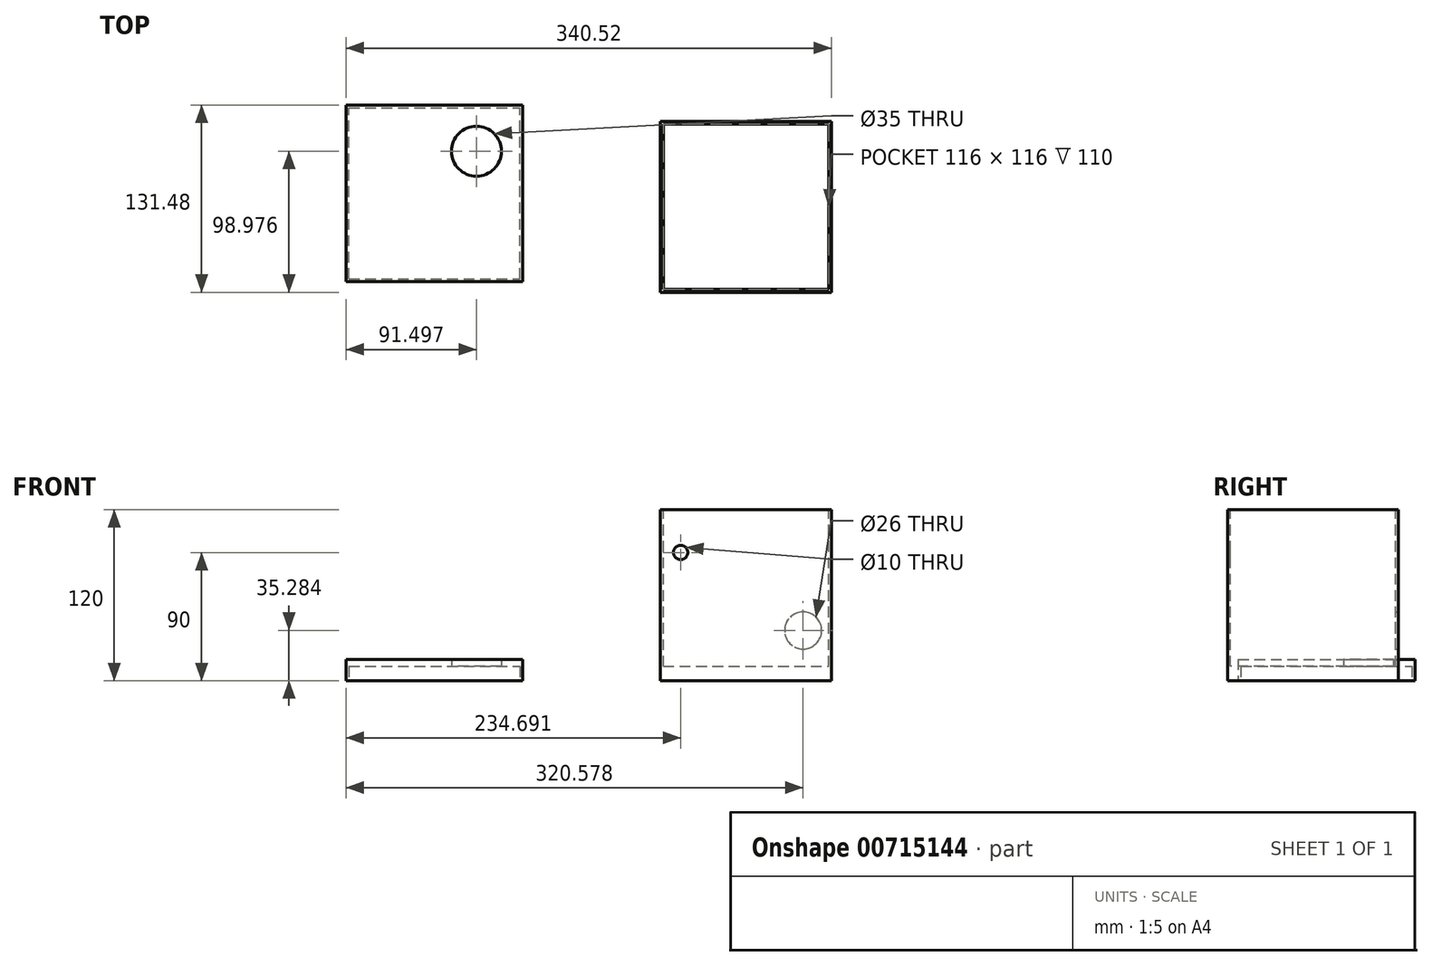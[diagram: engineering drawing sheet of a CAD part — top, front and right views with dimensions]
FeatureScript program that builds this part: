
annotation { "Feature Type Name" : "Feature", "Feature Type Description" : "" }
export const myFeature = defineFeature(function(context is Context, id is Id, definition is map)
    precondition{}
    {
        {
            var Q0;
            Q0=qCreatedBy(makeId("Top.planeOp"),FACE);
            var sketch = newSketch(context, id + "F0", { "sketchPlane" : qUnion([Q0])});
            skLineSegment(sketch, "E0.bottom", {"start": v(-59.8, 55.73) * mm, "end": v(60.2, 55.73) * mm});
            skLineSegment(sketch, "E0.top", {"start": v(-59.8, -64.27) * mm, "end": v(60.2, -64.27) * mm});
            skLineSegment(sketch, "E0.left", {"start": v(-59.8, 55.73) * mm, "end": v(-59.8, -64.27) * mm});
            skLineSegment(sketch, "E0.right", {"start": v(60.2, 55.73) * mm, "end": v(60.2, -64.27) * mm});
            skSolve(sketch);
        }
        {
            var Q0;
            Q0 = qSketchRegion(id + "F0", true);
            extrude(context, id + "F1", {"entities" : qUnion([Q0]), "depth" : 120 * mm, "offsetDistance" : 25 * mm});
        }
        {
            var Q0;
            Q0=makeQuery(id+"F1.opExtrude","CAP_FACE",FACE,{"disambiguationData":[OSD([sQuery(id+"F0.wireOp",EDGE,"E0.bottom"),sQuery(id+"F0.wireOp",EDGE,"E0.top"),sQuery(id+"F0.wireOp",EDGE,"E0.left"),sQuery(id+"F0.wireOp",EDGE,"E0.right")])],"isStart":false});
            var sketch = newSketch(context, id + "F2", { "sketchPlane" : qUnion([Q0])});
            skLineSegment(sketch, "E1.bottom", {"start": v(-57.8, 53.73) * mm, "end": v(58.2, 53.73) * mm});
            skLineSegment(sketch, "E1.top", {"start": v(-57.8, -62.27) * mm, "end": v(58.2, -62.27) * mm});
            skLineSegment(sketch, "E1.left", {"start": v(-57.8, 53.73) * mm, "end": v(-57.8, -62.27) * mm});
            skLineSegment(sketch, "E1.right", {"start": v(58.2, 53.73) * mm, "end": v(58.2, -62.27) * mm});
            skSolve(sketch);
        }
        {
            var Q0;
            Q0=makeQuery(id+"F2.imprint","IMPRINT",FACE,{"disambiguationData":[TD([[makeQuery(id+"F2.imprint","IMPRINT",EDGE,{"derivedFrom":sQuery(id+"F2.wireOp",EDGE,"E1.bottom")}),-1.0]])]});
            extrude(context, id + "F3", {"entities" : qUnion([Q0]), "operationType" : NewBodyOperationType.REMOVE, "oppositeDirection" : true, "depth" : 110 * mm, "offsetDistance" : 25 * mm});
        }
        {
            var Q0;
            Q0=makeQuery(id+"F1.opExtrude","SWEPT_FACE",FACE,{"disambiguationData":[OSD([sQuery(id+"F0.wireOp",EDGE,"E0.bottom")])]});
            var sketch = newSketch(context, id + "F4", { "sketchPlane" : qUnion([Q0])});
            skCircle(sketch, "E2", {"center": v(-40.26, 35.28) * mm, "radius": 13 * mm});
            skSolve(sketch);
        }
        {
            var Q0;
            Q0=makeQuery(id+"F4.imprint","IMPRINT",FACE,{"disambiguationData":[TD([[makeQuery(id+"F4.imprint","IMPRINT",EDGE,{"derivedFrom":sQuery(id+"F4.wireOp",EDGE,"E2")}),1.0]])]});
            extrude(context, id + "F5", {"entities" : qUnion([Q0]), "operationType" : NewBodyOperationType.REMOVE, "oppositeDirection" : true, "depth" : 25 * mm, "offsetDistance" : 25 * mm});
        }
        {
            var Q0;
            Q0=makeQuery(id+"F1.opExtrude","SWEPT_FACE",FACE,{"disambiguationData":[OSD([sQuery(id+"F0.wireOp",EDGE,"E0.top")])]});
            var sketch = newSketch(context, id + "F6", { "sketchPlane" : qUnion([Q0])});
            skCircle(sketch, "E3", {"center": v(-45.63, 90) * mm, "radius": 5 * mm});
            skSolve(sketch);
        }
        {
            var Q0;
            Q0 = qSketchRegion(id + "F6", true);
            extrude(context, id + "F7", {"entities" : qUnion([Q0]), "operationType" : NewBodyOperationType.REMOVE, "oppositeDirection" : true, "depth" : 25 * mm, "offsetDistance" : 25 * mm});
        }
        {
            var Q0;
            Q0=qCreatedBy(makeId("Top.planeOp"),FACE);
            var sketch = newSketch(context, id + "F8", { "sketchPlane" : qUnion([Q0])});
            skLineSegment(sketch, "E4.bottom", {"start": v(-156.32, -56.8) * mm, "end": v(-280.32, -56.8) * mm});
            skLineSegment(sketch, "E4.top", {"start": v(-156.32, 67.2) * mm, "end": v(-280.32, 67.2) * mm});
            skLineSegment(sketch, "E4.left", {"start": v(-156.32, -56.8) * mm, "end": v(-156.32, 67.2) * mm});
            skLineSegment(sketch, "E4.right", {"start": v(-280.32, -56.8) * mm, "end": v(-280.32, 67.2) * mm});
            skSolve(sketch);
        }
        {
            var Q0;
            Q0=makeQuery(id+"F8.imprint","IMPRINT",FACE,{"disambiguationData":[TD([[makeQuery(id+"F8.imprint","IMPRINT",EDGE,{"derivedFrom":sQuery(id+"F8.wireOp",EDGE,"E4.bottom")}),-1.0]])]});
            extrude(context, id + "F9", {"entities" : qUnion([Q0]), "depth" : 15 * mm, "offsetDistance" : 25 * mm});
        }
        {
            var Q0;
            Q0=qCreatedBy(makeId("Top.planeOp"),FACE);
            var sketch = newSketch(context, id + "F10", { "sketchPlane" : qUnion([Q0])});
            skLineSegment(sketch, "E5.bottom", {"start": v(-278.32, -54.8) * mm, "end": v(-158.32, -54.8) * mm});
            skLineSegment(sketch, "E5.top", {"start": v(-278.32, 65.2) * mm, "end": v(-158.32, 65.2) * mm});
            skLineSegment(sketch, "E5.left", {"start": v(-158.32, -54.8) * mm, "end": v(-158.32, 65.2) * mm});
            skLineSegment(sketch, "E5.right", {"start": v(-278.32, -54.8) * mm, "end": v(-278.32, 65.2) * mm});
            skSolve(sketch);
        }
        {
            var Q0;
            Q0 = qSketchRegion(id + "F10", true);
            extrude(context, id + "F11", {"entities" : qUnion([Q0]), "operationType" : NewBodyOperationType.REMOVE, "depth" : 10 * mm, "offsetDistance" : 25 * mm});
        }
        {
            var Q0;
            Q0=qCreatedBy(makeId("Top.planeOp"),FACE);
            var sketch = newSketch(context, id + "F12", { "sketchPlane" : qUnion([Q0])});
            skCircle(sketch, "E6", {"center": v(-188.82, 34.7) * mm, "radius": 17.5 * mm});
            skSolve(sketch);
        }
        {
            var Q0;
            Q0 = qSketchRegion(id + "F12", true);
            extrude(context, id + "F13", {"entities" : qUnion([Q0]), "operationType" : NewBodyOperationType.REMOVE, "depth" : 20 * mm, "offsetDistance" : 25 * mm});
        }
    });
